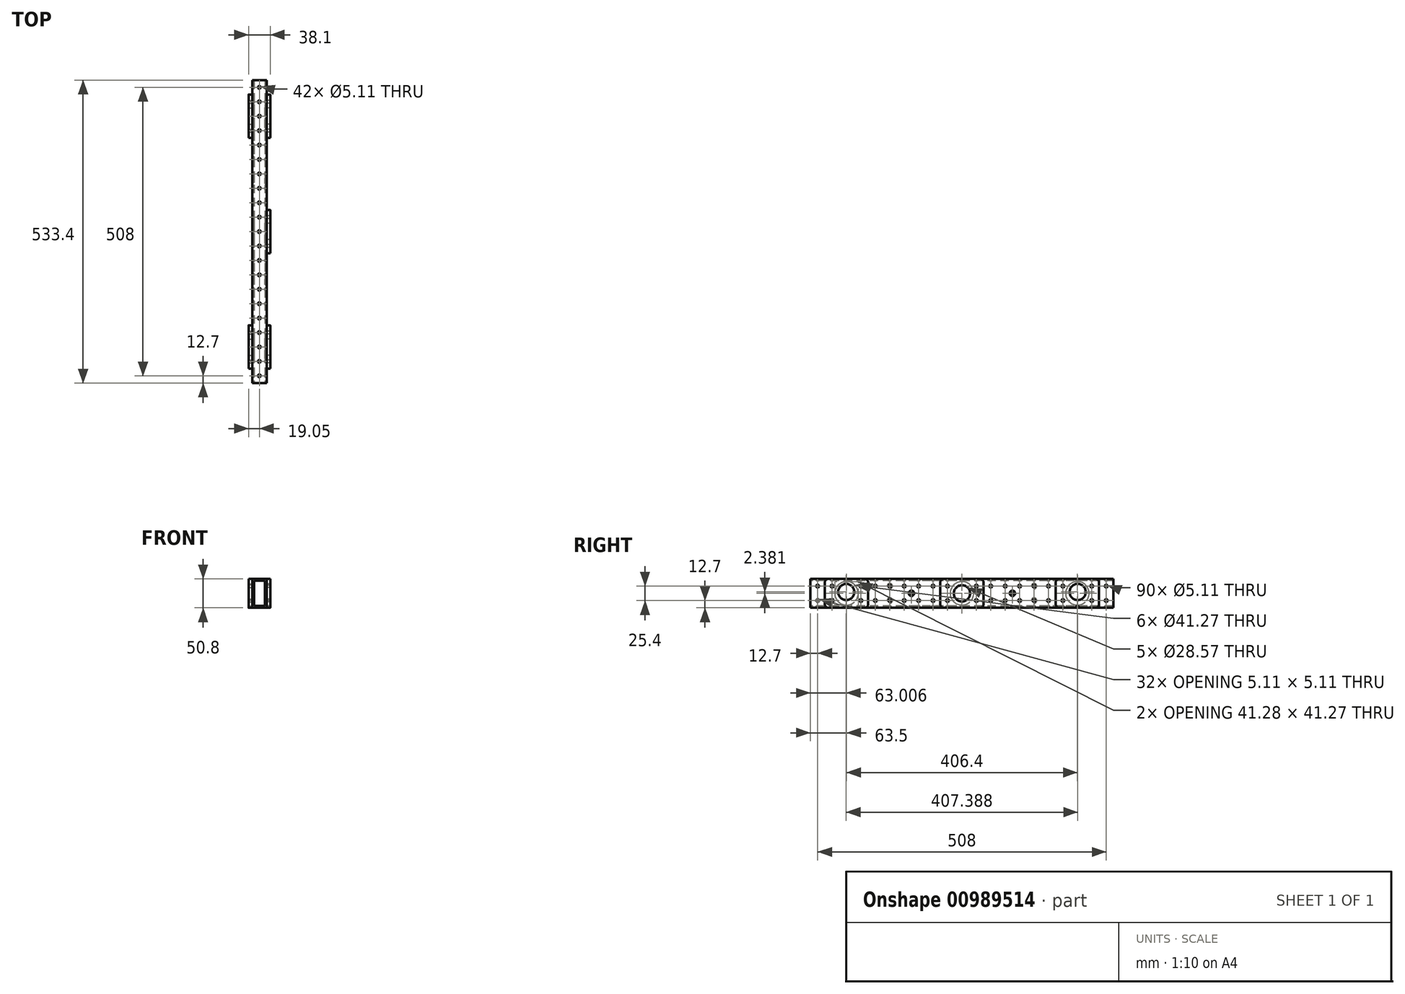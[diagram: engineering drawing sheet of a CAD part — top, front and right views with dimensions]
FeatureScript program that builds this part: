
annotation { "Feature Type Name" : "Feature", "Feature Type Description" : "" }
export const myFeature = defineFeature(function(context is Context, id is Id, definition is map)
    precondition{}
    {
        {
            var Q0;
            Q0=qCreatedBy(makeId("Right.planeOp"),FACE);
            var sketch = newSketch(context, id + "F0", { "sketchPlane" : qUnion([Q0])});
            skLineSegment(sketch, "E0.bottom", {"start": v(-266.7, 25.4) * mm, "end": v(266.7, 25.4) * mm});
            skLineSegment(sketch, "E0.top", {"start": v(-266.7, -25.4) * mm, "end": v(266.7, -25.4) * mm});
            skLineSegment(sketch, "E0.left", {"start": v(-266.7, 25.4) * mm, "end": v(-266.7, -25.4) * mm});
            skLineSegment(sketch, "E0.right", {"start": v(266.7, 25.4) * mm, "end": v(266.7, -25.4) * mm});
            skPoint(sketch, "E0.middle", {"position": v(0, 0) * mm});
            skCircle(sketch, "E1", {"center": v(-254, 12.7) * mm, "radius": 2.55 * mm});
            skCircle(sketch, "E2.0.1.0", {"center": v(-254, -12.7) * mm, "radius": 2.55 * mm});
            skCircle(sketch, "E2.1.0.0", {"center": v(-228.6, 12.7) * mm, "radius": 2.55 * mm});
            skCircle(sketch, "E2.1.1.0", {"center": v(-228.6, -12.7) * mm, "radius": 2.55 * mm});
            skCircle(sketch, "E2.2.0.0", {"center": v(-203.2, 12.7) * mm, "radius": 2.55 * mm});
            skCircle(sketch, "E2.2.1.0", {"center": v(-203.2, -12.7) * mm, "radius": 2.55 * mm});
            skCircle(sketch, "E2.3.0.0", {"center": v(-177.8, 12.7) * mm, "radius": 2.55 * mm});
            skCircle(sketch, "E2.3.1.0", {"center": v(-177.8, -12.7) * mm, "radius": 2.55 * mm});
            skCircle(sketch, "E2.4.0.0", {"center": v(-152.4, 12.7) * mm, "radius": 2.55 * mm});
            skCircle(sketch, "E2.4.1.0", {"center": v(-152.4, -12.7) * mm, "radius": 2.55 * mm});
            skCircle(sketch, "E2.5.0.0", {"center": v(-127, 12.7) * mm, "radius": 2.55 * mm});
            skCircle(sketch, "E2.5.1.0", {"center": v(-127, -12.7) * mm, "radius": 2.55 * mm});
            skCircle(sketch, "E2.6.0.0", {"center": v(-101.6, 12.7) * mm, "radius": 2.55 * mm});
            skCircle(sketch, "E2.6.1.0", {"center": v(-101.6, -12.7) * mm, "radius": 2.55 * mm});
            skCircle(sketch, "E2.7.0.0", {"center": v(-76.2, 12.7) * mm, "radius": 2.55 * mm});
            skCircle(sketch, "E2.7.1.0", {"center": v(-76.2, -12.7) * mm, "radius": 2.55 * mm});
            skCircle(sketch, "E2.8.0.0", {"center": v(-50.8, 12.7) * mm, "radius": 2.55 * mm});
            skCircle(sketch, "E2.8.1.0", {"center": v(-50.8, -12.7) * mm, "radius": 2.55 * mm});
            skCircle(sketch, "E2.9.0.0", {"center": v(-25.4, 12.7) * mm, "radius": 2.55 * mm});
            skCircle(sketch, "E2.9.1.0", {"center": v(-25.4, -12.7) * mm, "radius": 2.55 * mm});
            skCircle(sketch, "E2.10.0.0", {"center": v(0, 12.7) * mm, "radius": 2.55 * mm});
            skCircle(sketch, "E2.10.1.0", {"center": v(0, -12.7) * mm, "radius": 2.55 * mm});
            skCircle(sketch, "E2.11.0.0", {"center": v(25.4, 12.7) * mm, "radius": 2.55 * mm});
            skCircle(sketch, "E2.11.1.0", {"center": v(25.4, -12.7) * mm, "radius": 2.55 * mm});
            skCircle(sketch, "E2.12.0.0", {"center": v(50.8, 12.7) * mm, "radius": 2.55 * mm});
            skCircle(sketch, "E2.12.1.0", {"center": v(50.8, -12.7) * mm, "radius": 2.55 * mm});
            skCircle(sketch, "E2.13.0.0", {"center": v(76.2, 12.7) * mm, "radius": 2.55 * mm});
            skCircle(sketch, "E2.13.1.0", {"center": v(76.2, -12.7) * mm, "radius": 2.55 * mm});
            skCircle(sketch, "E2.14.0.0", {"center": v(101.6, 12.7) * mm, "radius": 2.55 * mm});
            skCircle(sketch, "E2.14.1.0", {"center": v(101.6, -12.7) * mm, "radius": 2.55 * mm});
            skCircle(sketch, "E2.15.0.0", {"center": v(127, 12.7) * mm, "radius": 2.55 * mm});
            skCircle(sketch, "E2.15.1.0", {"center": v(127, -12.7) * mm, "radius": 2.55 * mm});
            skCircle(sketch, "E2.16.0.0", {"center": v(152.4, 12.7) * mm, "radius": 2.55 * mm});
            skCircle(sketch, "E2.16.1.0", {"center": v(152.4, -12.7) * mm, "radius": 2.55 * mm});
            skCircle(sketch, "E2.17.0.0", {"center": v(177.8, 12.7) * mm, "radius": 2.55 * mm});
            skCircle(sketch, "E2.17.1.0", {"center": v(177.8, -12.7) * mm, "radius": 2.55 * mm});
            skCircle(sketch, "E2.18.0.0", {"center": v(203.2, 12.7) * mm, "radius": 2.55 * mm});
            skCircle(sketch, "E2.18.1.0", {"center": v(203.2, -12.7) * mm, "radius": 2.55 * mm});
            skCircle(sketch, "E2.19.0.0", {"center": v(228.6, 12.7) * mm, "radius": 2.55 * mm});
            skCircle(sketch, "E2.19.1.0", {"center": v(228.6, -12.7) * mm, "radius": 2.55 * mm});
            skCircle(sketch, "E2.20.0.0", {"center": v(254, 12.7) * mm, "radius": 2.55 * mm});
            skCircle(sketch, "E2.20.1.0", {"center": v(254, -12.7) * mm, "radius": 2.55 * mm});
            skLineSegment(sketch, "E2.direction1", {"start": v(-254, 12.7) * mm, "end": v(-228.6, 12.7) * mm, "construction": true});
            skLineSegment(sketch, "E2.direction2", {"start": v(-254, 12.7) * mm, "end": v(-254, -12.7) * mm, "construction": true});
            skLineSegment(sketch, "E3", {"start": v(-88.9, 0) * mm, "end": v(88.9, 0) * mm, "construction": true});
            skCircle(sketch, "E4", {"center": v(-88.9, 0) * mm, "radius": 2.55 * mm});
            skCircle(sketch, "E5", {"center": v(88.9, 0) * mm, "radius": 2.55 * mm});
            skCircle(sketch, "E6", {"center": v(0, 0) * mm, "radius": 20.64 * mm});
            skCircle(sketch, "E7", {"center": v(-203.2, 0) * mm, "radius": 50.8 * mm, "construction": true});
            skCircle(sketch, "E8", {"center": v(-203.2, 0) * mm, "radius": 20.64 * mm});
            skCircle(sketch, "E9", {"center": v(203.2, 0) * mm, "radius": 20.64 * mm});
            skSolve(sketch);
        }
        {
            var Q0;
            Q0 = qSketchRegion(id + "F0", true);
            extrude(context, id + "F1", {"entities" : qUnion([Q0]), "depth" : 12.7 * mm, "offsetDistance" : 25.4 * mm, "hasSecondDirection" : true, "secondDirectionOppositeDirection" : true, "secondDirectionDepth" : 12.7 * mm});
        }
        {
            var Q0;
            Q0=makeQuery(id+"F1.opExtrude","SWEPT_FACE",FACE,{"disambiguationData":[OSD([sQuery(id+"F0.wireOp",EDGE,"E0.left")])]});
            var sketch = newSketch(context, id + "F2", { "sketchPlane" : qUnion([Q0])});
            skLineSegment(sketch, "E10.0", {"start": v(9.53, 22.22) * mm, "end": v(-9.53, 22.22) * mm});
            skLineSegment(sketch, "E10.1", {"start": v(9.53, 22.22) * mm, "end": v(9.53, -22.22) * mm});
            skLineSegment(sketch, "E10.2", {"start": v(9.53, -22.23) * mm, "end": v(-9.53, -22.23) * mm});
            skLineSegment(sketch, "E10.3", {"start": v(-9.53, 22.22) * mm, "end": v(-9.53, -22.22) * mm});
            skSolve(sketch);
        }
        {
            var Q0;
            Q0 = qSketchRegion(id + "F2", true);
            extrude(context, id + "F3", {"entities" : qUnion([Q0]), "operationType" : NewBodyOperationType.REMOVE, "endBound" : BoundingType.THROUGH_ALL, "oppositeDirection" : true, "depth" : 25.4 * mm, "offsetDistance" : 25.4 * mm});
        }
        {
            var Q0;
            Q0=makeQuery(id+"F1.opExtrude","SWEPT_FACE",FACE,{"disambiguationData":[OSD([sQuery(id+"F0.wireOp",EDGE,"E0.bottom")])]});
            var sketch = newSketch(context, id + "F4", { "sketchPlane" : qUnion([Q0])});
            skCircle(sketch, "E11", {"center": v(0, 254) * mm, "radius": 2.55 * mm});
            skCircle(sketch, "E12.0.1.0", {"center": v(0, 228.6) * mm, "radius": 2.55 * mm});
            skCircle(sketch, "E12.0.2.0", {"center": v(0, 203.2) * mm, "radius": 2.55 * mm});
            skCircle(sketch, "E12.0.3.0", {"center": v(0, 177.8) * mm, "radius": 2.55 * mm});
            skCircle(sketch, "E12.0.4.0", {"center": v(0, 152.4) * mm, "radius": 2.55 * mm});
            skCircle(sketch, "E12.0.5.0", {"center": v(0, 127) * mm, "radius": 2.55 * mm});
            skCircle(sketch, "E12.0.6.0", {"center": v(0, 101.6) * mm, "radius": 2.55 * mm});
            skCircle(sketch, "E12.0.7.0", {"center": v(0, 76.2) * mm, "radius": 2.55 * mm});
            skCircle(sketch, "E12.0.8.0", {"center": v(0, 50.8) * mm, "radius": 2.55 * mm});
            skCircle(sketch, "E12.0.9.0", {"center": v(0, 25.4) * mm, "radius": 2.55 * mm});
            skCircle(sketch, "E12.0.10.0", {"center": v(0, 0) * mm, "radius": 2.55 * mm});
            skCircle(sketch, "E12.0.11.0", {"center": v(0, -25.4) * mm, "radius": 2.55 * mm});
            skCircle(sketch, "E12.0.12.0", {"center": v(0, -50.8) * mm, "radius": 2.55 * mm});
            skCircle(sketch, "E12.0.13.0", {"center": v(0, -76.2) * mm, "radius": 2.55 * mm});
            skCircle(sketch, "E12.0.14.0", {"center": v(0, -101.6) * mm, "radius": 2.55 * mm});
            skCircle(sketch, "E12.0.15.0", {"center": v(0, -127) * mm, "radius": 2.55 * mm});
            skCircle(sketch, "E12.0.16.0", {"center": v(0, -152.4) * mm, "radius": 2.55 * mm});
            skCircle(sketch, "E12.0.17.0", {"center": v(0, -177.8) * mm, "radius": 2.55 * mm});
            skCircle(sketch, "E12.0.18.0", {"center": v(0, -203.2) * mm, "radius": 2.55 * mm});
            skCircle(sketch, "E12.0.19.0", {"center": v(0, -228.6) * mm, "radius": 2.55 * mm});
            skCircle(sketch, "E12.0.20.0", {"center": v(0, -254) * mm, "radius": 2.55 * mm});
            skLineSegment(sketch, "E12.direction1", {"start": v(0, 254) * mm, "end": v(38.1, 254) * mm, "construction": true});
            skLineSegment(sketch, "E12.direction2", {"start": v(0, 254) * mm, "end": v(0, 228.6) * mm, "construction": true});
            skSolve(sketch);
        }
        {
            var Q0;
            Q0 = qSketchRegion(id + "F4", true);
            extrude(context, id + "F5", {"entities" : qUnion([Q0]), "operationType" : NewBodyOperationType.REMOVE, "endBound" : BoundingType.THROUGH_ALL, "oppositeDirection" : true, "depth" : 25.4 * mm, "offsetDistance" : 25.4 * mm});
        }
        {
            var Q0;
            Q0=makeQuery(id+"F1.opExtrude","CAP_FACE",FACE,{"disambiguationData":[OSD([sQuery(id+"F0.wireOp",EDGE,"E0.bottom"),sQuery(id+"F0.wireOp",EDGE,"E0.top"),sQuery(id+"F0.wireOp",EDGE,"E0.left"),sQuery(id+"F0.wireOp",EDGE,"E0.right"),sQuery(id+"F0.wireOp",EDGE,"E1"),sQuery(id+"F0.wireOp",EDGE,"E2.0.1.0"),sQuery(id+"F0.wireOp",EDGE,"E2.1.0.0"),sQuery(id+"F0.wireOp",EDGE,"E2.1.1.0"),sQuery(id+"F0.wireOp",EDGE,"E2.3.0.0"),sQuery(id+"F0.wireOp",EDGE,"E2.3.1.0"),sQuery(id+"F0.wireOp",EDGE,"E2.4.0.0"),sQuery(id+"F0.wireOp",EDGE,"E2.4.1.0"),sQuery(id+"F0.wireOp",EDGE,"E2.5.0.0"),sQuery(id+"F0.wireOp",EDGE,"E2.5.1.0"),sQuery(id+"F0.wireOp",EDGE,"E2.6.0.0"),sQuery(id+"F0.wireOp",EDGE,"E2.6.1.0"),sQuery(id+"F0.wireOp",EDGE,"E2.7.0.0"),sQuery(id+"F0.wireOp",EDGE,"E2.7.1.0"),sQuery(id+"F0.wireOp",EDGE,"E2.8.0.0"),sQuery(id+"F0.wireOp",EDGE,"E2.8.1.0"),sQuery(id+"F0.wireOp",EDGE,"E2.9.0.0"),sQuery(id+"F0.wireOp",EDGE,"E2.9.1.0"),sQuery(id+"F0.wireOp",EDGE,"E2.11.0.0"),sQuery(id+"F0.wireOp",EDGE,"E2.11.1.0"),sQuery(id+"F0.wireOp",EDGE,"E2.12.0.0"),sQuery(id+"F0.wireOp",EDGE,"E2.12.1.0"),sQuery(id+"F0.wireOp",EDGE,"E2.13.0.0"),sQuery(id+"F0.wireOp",EDGE,"E2.13.1.0"),sQuery(id+"F0.wireOp",EDGE,"E2.14.0.0"),sQuery(id+"F0.wireOp",EDGE,"E2.14.1.0"),sQuery(id+"F0.wireOp",EDGE,"E2.15.0.0"),sQuery(id+"F0.wireOp",EDGE,"E2.15.1.0"),sQuery(id+"F0.wireOp",EDGE,"E2.16.0.0"),sQuery(id+"F0.wireOp",EDGE,"E2.16.1.0"),sQuery(id+"F0.wireOp",EDGE,"E2.17.0.0"),sQuery(id+"F0.wireOp",EDGE,"E2.17.1.0"),sQuery(id+"F0.wireOp",EDGE,"E2.19.0.0"),sQuery(id+"F0.wireOp",EDGE,"E2.19.1.0"),sQuery(id+"F0.wireOp",EDGE,"E2.20.0.0"),sQuery(id+"F0.wireOp",EDGE,"E2.20.1.0"),sQuery(id+"F0.wireOp",EDGE,"E4"),sQuery(id+"F0.wireOp",EDGE,"E5"),sQuery(id+"F0.wireOp",EDGE,"E6"),sQuery(id+"F0.wireOp",EDGE,"E8"),sQuery(id+"F0.wireOp",EDGE,"E9")])],"isStart":false});
            var sketch = newSketch(context, id + "F6", { "sketchPlane" : qUnion([Q0])});
            skLineSegment(sketch, "E13.bottom", {"start": v(-31.75, 25.4) * mm, "end": v(31.75, 25.4) * mm});
            skLineSegment(sketch, "E13.top", {"start": v(-31.75, -25.4) * mm, "end": v(31.75, -25.4) * mm});
            skLineSegment(sketch, "E13.left", {"start": v(-38.1, 19.05) * mm, "end": v(-38.1, -19.05) * mm});
            skLineSegment(sketch, "E13.right", {"start": v(38.1, 19.05) * mm, "end": v(38.1, -19.05) * mm});
            skPoint(sketch, "E13.middle", {"position": v(0, 0) * mm});
            skCircle(sketch, "E14", {"center": v(0, 0) * mm, "radius": 14.29 * mm});
            skPoint(sketch, "E15.visualSharp", {"position": v(-38.1, 25.4) * mm});
            skArc(sketch, "E15.filletArc", {"start": v(-31.75, 25.4) * mm, "mid": v(-36.24, 23.54) * mm, "end": v(-38.1, 19.05) * mm});
            skPoint(sketch, "E16.visualSharp", {"position": v(38.1, -25.4) * mm});
            skArc(sketch, "E16.filletArc", {"start": v(31.75, -25.4) * mm, "mid": v(36.24, -23.54) * mm, "end": v(38.1, -19.05) * mm});
            skPoint(sketch, "E17.visualSharp", {"position": v(38.1, 25.4) * mm});
            skArc(sketch, "E17.filletArc", {"start": v(38.1, 19.05) * mm, "mid": v(36.24, 23.54) * mm, "end": v(31.75, 25.4) * mm});
            skPoint(sketch, "E18.visualSharp", {"position": v(-38.1, -25.4) * mm});
            skArc(sketch, "E18.filletArc", {"start": v(-38.1, -19.05) * mm, "mid": v(-36.24, -23.54) * mm, "end": v(-31.75, -25.4) * mm});
            skCircle(sketch, "E19", {"center": v(-25.4, 12.7) * mm, "radius": 2.55 * mm});
            skCircle(sketch, "E20", {"center": v(-25.4, -12.7) * mm, "radius": 2.55 * mm});
            skCircle(sketch, "E21", {"center": v(25.4, -12.7) * mm, "radius": 2.55 * mm});
            skCircle(sketch, "E22", {"center": v(25.4, 12.7) * mm, "radius": 2.55 * mm});
            skLineSegment(sketch, "E23", {"start": v(0, 0) * mm, "end": v(-203.7, 2.38) * mm, "construction": true});
            skCircle(sketch, "E24", {"center": v(-203.7, 2.38) * mm, "radius": 14.29 * mm});
            skCircle(sketch, "E25", {"center": v(203.7, 2.38) * mm, "radius": 14.29 * mm});
            skLineSegment(sketch, "E26", {"start": v(0, 0) * mm, "end": v(203.7, 2.38) * mm, "construction": true});
            skLineSegment(sketch, "E27.bottom", {"start": v(-171.45, 25.4) * mm, "end": v(-234.95, 25.4) * mm});
            skLineSegment(sketch, "E27.left", {"start": v(-165.1, 19.05) * mm, "end": v(-165.1, -19.05) * mm});
            skLineSegment(sketch, "E27.right", {"start": v(-241.3, 19.05) * mm, "end": v(-241.3, -19.05) * mm});
            skPoint(sketch, "E27.middle", {"position": v(-203.2, 0) * mm});
            skPoint(sketch, "E28.visualSharp", {"position": v(-241.3, 25.4) * mm});
            skArc(sketch, "E28.filletArc", {"start": v(-234.95, 25.4) * mm, "mid": v(-239.44, 23.54) * mm, "end": v(-241.3, 19.05) * mm});
            skPoint(sketch, "E29.visualSharp", {"position": v(-165.1, 25.4) * mm});
            skArc(sketch, "E29.filletArc", {"start": v(-165.1, 19.05) * mm, "mid": v(-166.96, 23.54) * mm, "end": v(-171.45, 25.4) * mm});
            skPoint(sketch, "E30.visualSharp", {"position": v(-165.1, -25.4) * mm});
            skArc(sketch, "E30.filletArc", {"start": v(-171.45, -25.4) * mm, "mid": v(-166.96, -23.54) * mm, "end": v(-165.1, -19.05) * mm});
            skPoint(sketch, "E31.visualSharp", {"position": v(-241.3, -25.4) * mm});
            skArc(sketch, "E31.filletArc", {"start": v(-241.3, -19.05) * mm, "mid": v(-239.44, -23.54) * mm, "end": v(-234.95, -25.4) * mm});
            skCircle(sketch, "E32", {"center": v(-228.6, 12.7) * mm, "radius": 2.55 * mm});
            skCircle(sketch, "E33", {"center": v(-177.8, 12.7) * mm, "radius": 2.55 * mm});
            skCircle(sketch, "E34", {"center": v(-177.8, -12.7) * mm, "radius": 2.55 * mm});
            skCircle(sketch, "E35", {"center": v(-228.6, -12.7) * mm, "radius": 2.55 * mm});
            skLineSegment(sketch, "E36", {"start": v(-234.95, -25.4) * mm, "end": v(-208.7, -25.4) * mm});
            skLineSegment(sketch, "E37", {"start": v(-171.45, -25.4) * mm, "end": v(-197.7, -25.4) * mm});
            skArc(sketch, "E38", {"start": v(-200.45, -23.81) * mm, "mid": v(-203.2, -22.22) * mm, "end": v(-205.95, -23.81) * mm});
            skPoint(sketch, "E39.visualSharp", {"position": v(-200.02, -25.4) * mm});
            skArc(sketch, "E39.filletArc", {"start": v(-200.45, -23.81) * mm, "mid": v(-199.29, -24.97) * mm, "end": v(-197.7, -25.4) * mm});
            skPoint(sketch, "E40.visualSharp", {"position": v(-206.38, -25.4) * mm});
            skArc(sketch, "E40.filletArc", {"start": v(-208.7, -25.4) * mm, "mid": v(-207.11, -24.97) * mm, "end": v(-205.95, -23.81) * mm});
            skArc(sketch, "E41.MirrorCS", {"start": v(200.45, -23.81) * mm, "mid": v(199.29, -24.97) * mm, "end": v(197.7, -25.4) * mm});
            skArc(sketch, "E42.MirrorCS", {"start": v(200.45, -23.81) * mm, "mid": v(203.2, -22.22) * mm, "end": v(205.95, -23.81) * mm});
            skArc(sketch, "E43.MirrorCS", {"start": v(208.7, -25.4) * mm, "mid": v(207.11, -24.97) * mm, "end": v(205.95, -23.81) * mm});
            skCircle(sketch, "E44.MirrorC", {"center": v(177.8, 12.7) * mm, "radius": 2.55 * mm});
            skPoint(sketch, "E45.MirrorP", {"position": v(200.02, -25.4) * mm});
            skLineSegment(sketch, "E46.MirrorCS", {"start": v(234.95, -25.4) * mm, "end": v(208.7, -25.4) * mm});
            skPoint(sketch, "E47.MirrorP", {"position": v(203.2, 0) * mm});
            skPoint(sketch, "E48.MirrorP", {"position": v(241.3, 25.4) * mm});
            skArc(sketch, "E49.MirrorCS", {"start": v(165.1, 19.05) * mm, "mid": v(166.96, 23.54) * mm, "end": v(171.45, 25.4) * mm});
            skCircle(sketch, "E50.MirrorC", {"center": v(228.6, -12.7) * mm, "radius": 2.55 * mm});
            skArc(sketch, "E51.MirrorCS", {"start": v(234.95, 25.4) * mm, "mid": v(239.44, 23.54) * mm, "end": v(241.3, 19.05) * mm});
            skPoint(sketch, "E52.MirrorP", {"position": v(165.1, -25.4) * mm});
            skArc(sketch, "E53.MirrorCS", {"start": v(171.45, -25.4) * mm, "mid": v(166.96, -23.54) * mm, "end": v(165.1, -19.05) * mm});
            skPoint(sketch, "E54.MirrorP", {"position": v(206.38, -25.4) * mm});
            skPoint(sketch, "E55.MirrorP", {"position": v(165.1, 25.4) * mm});
            skPoint(sketch, "E56.MirrorP", {"position": v(241.3, -25.4) * mm});
            skArc(sketch, "E57.MirrorCS", {"start": v(241.3, -19.05) * mm, "mid": v(239.44, -23.54) * mm, "end": v(234.95, -25.4) * mm});
            skLineSegment(sketch, "E58.MirrorCS", {"start": v(241.3, 19.05) * mm, "end": v(241.3, -19.05) * mm});
            skLineSegment(sketch, "E59.MirrorCS", {"start": v(165.1, 19.05) * mm, "end": v(165.1, -19.05) * mm});
            skLineSegment(sketch, "E60.MirrorCS", {"start": v(171.45, -25.4) * mm, "end": v(197.7, -25.4) * mm});
            skCircle(sketch, "E61.MirrorC", {"center": v(228.6, 12.7) * mm, "radius": 2.55 * mm});
            skLineSegment(sketch, "E62.MirrorCS", {"start": v(171.45, 25.4) * mm, "end": v(234.95, 25.4) * mm});
            skCircle(sketch, "E63.MirrorC", {"center": v(177.8, -12.7) * mm, "radius": 2.55 * mm});
            skSolve(sketch);
        }
        {
            var Q0;
            Q0 = qSketchRegion(id + "F6", true);
            extrude(context, id + "F7", {"entities" : qUnion([Q0]), "depth" : 6.35 * mm, "offsetDistance" : 25.4 * mm});
        }
        {
            var Q0;
            Q0=makeQuery(id+"F7.opExtrude","SWEPT_BODY",BODY,{"disambiguationData":[OSD([sQuery(id+"F6.wireOp",EDGE,"E24"),sQuery(id+"F6.wireOp",EDGE,"E27.bottom"),sQuery(id+"F6.wireOp",EDGE,"E27.left"),sQuery(id+"F6.wireOp",EDGE,"E27.right"),sQuery(id+"F6.wireOp",EDGE,"E28.filletArc"),sQuery(id+"F6.wireOp",EDGE,"E29.filletArc"),sQuery(id+"F6.wireOp",EDGE,"E30.filletArc"),sQuery(id+"F6.wireOp",EDGE,"E31.filletArc"),sQuery(id+"F6.wireOp",EDGE,"E32"),sQuery(id+"F6.wireOp",EDGE,"E33"),sQuery(id+"F6.wireOp",EDGE,"E34"),sQuery(id+"F6.wireOp",EDGE,"E35"),sQuery(id+"F6.wireOp",EDGE,"E36"),sQuery(id+"F6.wireOp",EDGE,"E37"),sQuery(id+"F6.wireOp",EDGE,"E38"),sQuery(id+"F6.wireOp",EDGE,"E39.filletArc"),sQuery(id+"F6.wireOp",EDGE,"E40.filletArc")])]});
            var Q1;
            Q1=makeQuery(id+"F7.opExtrude","SWEPT_BODY",BODY,{"disambiguationData":[OSD([sQuery(id+"F6.wireOp",EDGE,"E41.MirrorCS"),sQuery(id+"F6.wireOp",EDGE,"E42.MirrorCS"),sQuery(id+"F6.wireOp",EDGE,"E43.MirrorCS"),sQuery(id+"F6.wireOp",EDGE,"E44.MirrorC"),sQuery(id+"F6.wireOp",EDGE,"E46.MirrorCS"),sQuery(id+"F6.wireOp",EDGE,"E49.MirrorCS"),sQuery(id+"F6.wireOp",EDGE,"E50.MirrorC"),sQuery(id+"F6.wireOp",EDGE,"E51.MirrorCS"),sQuery(id+"F6.wireOp",EDGE,"E53.MirrorCS"),sQuery(id+"F6.wireOp",EDGE,"E57.MirrorCS"),sQuery(id+"F6.wireOp",EDGE,"E58.MirrorCS"),sQuery(id+"F6.wireOp",EDGE,"E59.MirrorCS"),sQuery(id+"F6.wireOp",EDGE,"E60.MirrorCS"),sQuery(id+"F6.wireOp",EDGE,"E25"),sQuery(id+"F6.wireOp",EDGE,"E61.MirrorC"),sQuery(id+"F6.wireOp",EDGE,"E62.MirrorCS"),sQuery(id+"F6.wireOp",EDGE,"E63.MirrorC")])]});
            var Q2;
            Q2=qCreatedBy(makeId("Right.planeOp"),FACE);
            mirror(context, id + "F8", {"entities" : qUnion([Q0, Q1]), "mirrorPlane" : qUnion([Q2])});
        }
        {
            var Q0;
            Q0=makeQuery(id+"F1.opExtrude","CAP_FACE",FACE,{"disambiguationData":[OSD([sQuery(id+"F0.wireOp",EDGE,"E0.bottom"),sQuery(id+"F0.wireOp",EDGE,"E0.top"),sQuery(id+"F0.wireOp",EDGE,"E0.left"),sQuery(id+"F0.wireOp",EDGE,"E0.right"),sQuery(id+"F0.wireOp",EDGE,"E1"),sQuery(id+"F0.wireOp",EDGE,"E2.0.1.0"),sQuery(id+"F0.wireOp",EDGE,"E2.1.0.0"),sQuery(id+"F0.wireOp",EDGE,"E2.1.1.0"),sQuery(id+"F0.wireOp",EDGE,"E2.3.0.0"),sQuery(id+"F0.wireOp",EDGE,"E2.3.1.0"),sQuery(id+"F0.wireOp",EDGE,"E2.4.0.0"),sQuery(id+"F0.wireOp",EDGE,"E2.4.1.0"),sQuery(id+"F0.wireOp",EDGE,"E2.5.0.0"),sQuery(id+"F0.wireOp",EDGE,"E2.5.1.0"),sQuery(id+"F0.wireOp",EDGE,"E2.6.0.0"),sQuery(id+"F0.wireOp",EDGE,"E2.6.1.0"),sQuery(id+"F0.wireOp",EDGE,"E2.7.0.0"),sQuery(id+"F0.wireOp",EDGE,"E2.7.1.0"),sQuery(id+"F0.wireOp",EDGE,"E2.8.0.0"),sQuery(id+"F0.wireOp",EDGE,"E2.8.1.0"),sQuery(id+"F0.wireOp",EDGE,"E2.9.0.0"),sQuery(id+"F0.wireOp",EDGE,"E2.9.1.0"),sQuery(id+"F0.wireOp",EDGE,"E2.11.0.0"),sQuery(id+"F0.wireOp",EDGE,"E2.11.1.0"),sQuery(id+"F0.wireOp",EDGE,"E2.12.0.0"),sQuery(id+"F0.wireOp",EDGE,"E2.12.1.0"),sQuery(id+"F0.wireOp",EDGE,"E2.13.0.0"),sQuery(id+"F0.wireOp",EDGE,"E2.13.1.0"),sQuery(id+"F0.wireOp",EDGE,"E2.14.0.0"),sQuery(id+"F0.wireOp",EDGE,"E2.14.1.0"),sQuery(id+"F0.wireOp",EDGE,"E2.15.0.0"),sQuery(id+"F0.wireOp",EDGE,"E2.15.1.0"),sQuery(id+"F0.wireOp",EDGE,"E2.16.0.0"),sQuery(id+"F0.wireOp",EDGE,"E2.16.1.0"),sQuery(id+"F0.wireOp",EDGE,"E2.17.0.0"),sQuery(id+"F0.wireOp",EDGE,"E2.17.1.0"),sQuery(id+"F0.wireOp",EDGE,"E2.19.0.0"),sQuery(id+"F0.wireOp",EDGE,"E2.19.1.0"),sQuery(id+"F0.wireOp",EDGE,"E2.20.0.0"),sQuery(id+"F0.wireOp",EDGE,"E2.20.1.0"),sQuery(id+"F0.wireOp",EDGE,"E4"),sQuery(id+"F0.wireOp",EDGE,"E5"),sQuery(id+"F0.wireOp",EDGE,"E6"),sQuery(id+"F0.wireOp",EDGE,"E8"),sQuery(id+"F0.wireOp",EDGE,"E9")])],"isStart":false});
            var sketch = newSketch(context, id + "F9", { "sketchPlane" : qUnion([Q0])});
            skCircle(sketch, "E64", {"center": v(-88.9, 0) * mm, "radius": 4.76 * mm});
            skCircle(sketch, "E65", {"center": v(88.9, 0) * mm, "radius": 4.76 * mm});
            skSolve(sketch);
        }
        {
            var Q0;
            Q0 = qSketchRegion(id + "F9", true);
            extrude(context, id + "F10", {"entities" : qUnion([Q0]), "operationType" : NewBodyOperationType.REMOVE, "oppositeDirection" : true, "depth" : 3.17 * mm, "offsetDistance" : 25.4 * mm});
        }
        {
            var Q0;
            Q0=makeQuery(id+"F1.opExtrude","CAP_FACE",FACE,{"disambiguationData":[OSD([sQuery(id+"F0.wireOp",EDGE,"E0.bottom"),sQuery(id+"F0.wireOp",EDGE,"E0.top"),sQuery(id+"F0.wireOp",EDGE,"E0.left"),sQuery(id+"F0.wireOp",EDGE,"E0.right"),sQuery(id+"F0.wireOp",EDGE,"E1"),sQuery(id+"F0.wireOp",EDGE,"E2.0.1.0"),sQuery(id+"F0.wireOp",EDGE,"E2.1.0.0"),sQuery(id+"F0.wireOp",EDGE,"E2.1.1.0"),sQuery(id+"F0.wireOp",EDGE,"E2.3.0.0"),sQuery(id+"F0.wireOp",EDGE,"E2.3.1.0"),sQuery(id+"F0.wireOp",EDGE,"E2.4.0.0"),sQuery(id+"F0.wireOp",EDGE,"E2.4.1.0"),sQuery(id+"F0.wireOp",EDGE,"E2.5.0.0"),sQuery(id+"F0.wireOp",EDGE,"E2.5.1.0"),sQuery(id+"F0.wireOp",EDGE,"E2.6.0.0"),sQuery(id+"F0.wireOp",EDGE,"E2.6.1.0"),sQuery(id+"F0.wireOp",EDGE,"E2.7.0.0"),sQuery(id+"F0.wireOp",EDGE,"E2.7.1.0"),sQuery(id+"F0.wireOp",EDGE,"E2.8.0.0"),sQuery(id+"F0.wireOp",EDGE,"E2.8.1.0"),sQuery(id+"F0.wireOp",EDGE,"E2.9.0.0"),sQuery(id+"F0.wireOp",EDGE,"E2.9.1.0"),sQuery(id+"F0.wireOp",EDGE,"E2.11.0.0"),sQuery(id+"F0.wireOp",EDGE,"E2.11.1.0"),sQuery(id+"F0.wireOp",EDGE,"E2.12.0.0"),sQuery(id+"F0.wireOp",EDGE,"E2.12.1.0"),sQuery(id+"F0.wireOp",EDGE,"E2.13.0.0"),sQuery(id+"F0.wireOp",EDGE,"E2.13.1.0"),sQuery(id+"F0.wireOp",EDGE,"E2.14.0.0"),sQuery(id+"F0.wireOp",EDGE,"E2.14.1.0"),sQuery(id+"F0.wireOp",EDGE,"E2.15.0.0"),sQuery(id+"F0.wireOp",EDGE,"E2.15.1.0"),sQuery(id+"F0.wireOp",EDGE,"E2.16.0.0"),sQuery(id+"F0.wireOp",EDGE,"E2.16.1.0"),sQuery(id+"F0.wireOp",EDGE,"E2.17.0.0"),sQuery(id+"F0.wireOp",EDGE,"E2.17.1.0"),sQuery(id+"F0.wireOp",EDGE,"E2.19.0.0"),sQuery(id+"F0.wireOp",EDGE,"E2.19.1.0"),sQuery(id+"F0.wireOp",EDGE,"E2.20.0.0"),sQuery(id+"F0.wireOp",EDGE,"E2.20.1.0"),sQuery(id+"F0.wireOp",EDGE,"E4"),sQuery(id+"F0.wireOp",EDGE,"E5"),sQuery(id+"F0.wireOp",EDGE,"E6"),sQuery(id+"F0.wireOp",EDGE,"E8"),sQuery(id+"F0.wireOp",EDGE,"E9")])],"isStart":true});
            var sketch = newSketch(context, id + "F11", { "sketchPlane" : qUnion([Q0])});
            skCircle(sketch, "E66", {"center": v(-127, 12.7) * mm, "radius": 4.76 * mm});
            skCircle(sketch, "E67", {"center": v(-127, -12.7) * mm, "radius": 4.76 * mm});
            skCircle(sketch, "E68", {"center": v(127, 12.7) * mm, "radius": 4.76 * mm});
            skCircle(sketch, "E69", {"center": v(127, -12.7) * mm, "radius": 4.76 * mm});
            skSolve(sketch);
        }
        {
            var Q0;
            Q0 = qSketchRegion(id + "F11", true);
            extrude(context, id + "F12", {"entities" : qUnion([Q0]), "operationType" : NewBodyOperationType.REMOVE, "oppositeDirection" : true, "depth" : 3.17 * mm, "offsetDistance" : 25.4 * mm});
        }
    });
